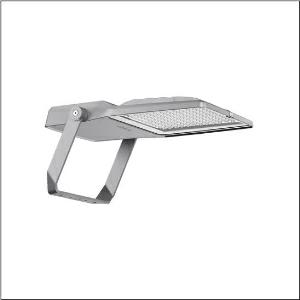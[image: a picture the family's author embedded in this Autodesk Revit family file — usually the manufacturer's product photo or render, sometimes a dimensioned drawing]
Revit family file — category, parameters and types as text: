
# Revit family: floodlight_fl_21_iq_midi___rs12_5xa7782f4b1a_76e1
name_source: partatom
category: Lighting Fixtures
units: mm (PartAtom-declared; Revit-internal decimal feet)

## family parameters
Cut with Voids When Loaded = No
Host = Face
Light Source = No
Part Type = Normal
Room Calculation Point = No
Round Connector Dimension = Use Diameter
Shared = No

## types (1)
- --- (1 x LED, 37160 lm, 270.2 W, 4000K)
    Apparent Load = 270 VA
    CIE Flux Codes = 79 92 99 100 100
    Color Rendering = 70
    Color Temperature = 4000K
    Default Elevation = 1800 mm
    Description = Floodlight FL 21 iQ midi, floodlight, primary light control with lens, of PMMA, primary optical cover: protective disc, of toughened safety glass, transparent, light distribution: RS12, light emission: direct distribution, installation type: surface-mounted, LED, High Power LED, rated luminous flux: 37.160lm, luminous efficacy: 138lm/W, light colour: 740, colour temperature: 4000K, control gear: ECG iQ, control: optimised constant luminous flux control (CLO 2.0), Desk-Remote (wireless, voltage-free reading and setting of iQ features in the workshop via application-optimized NFC function/RFID function), Smart-Wire, Night-Set, Temp-Guard, Street-Remote, Auto-Match, with terminal, 6-pole, mains connection: 220..240V, AC, 50/60Hz, start of lifetime: 270W, end of service life: 287W, reduction: 118W, luminaire housing, of diecast aluminium, powder-coated, Siteco® metallic grey (DB 702S), corrosivity category C5 mid according to DIN EN ISO 12944, sealing non-destructively replaceable, mounting bracket, of steel, galvanised, powder-coated, Siteco® metallic grey (DB 702S), protection rating (complete): IP66, insulation class (complete): insulation class II (safety insulation), certification: CE, protection symbol: D, impact resistance: IK08, permissible operating ambient temperature: -40..+40°C, permissible operating ambient temperature for outdoor applications: -40..+50°C, standard: DIN EN 12944, LABS conformity tested according to VDMA 24364:2018-05, packaging unit: 1 piece

Light Distribution: RS12
    Height = 76 mm
    Lamp = 1 x LED
    Lamp Light Flux = 37160 lm
    Lamp Power = 270.2 W
    Lamp count = 1
    Length = 657 mm
    Luminous efficacy = 138 lm/W
    Manufacturer = Siteco
    ModVariant = No
    Model = 5XA7782F4B1A
    Number of Poles = 1
    OnlyDefault = Yes
    Power Factor = 1
    Product Name = Floodlight FL 21 iQ midi | RS12
    Product group = floodlight | pylon annexe
    ProductGroupID = 6200
    Protection Class = Protection class II
    Protection Degree = IP 66
    RLX_Detail_Level = 1
    RLX_Emergency_Light_Flux = 0 lm
    RLX_Emergency_Type = 0
    RLX_Emergency_Type_DB = No
    RlxData = <blob elided: 141349 chars, md5=35fc69df>
    Socket = socket
    Standby Power = 0 W
    System Light Flux = 37160 lm
    System Power = 270 W
    Type Comments = factory setting: luminous flux: 100 % | dim-lin: 254 | 620 mA
    Type Image = l_1006876.jpg
    URL = http://relux.com
    VarID = @adj_055723
    Voltage = 0 V
    Weight = 0.00 kg
    Width = 442 mm

## geometry (parser evidence)
native form markers: Blend x4, Sweep x12
no freeform markers — native parametric forms only
